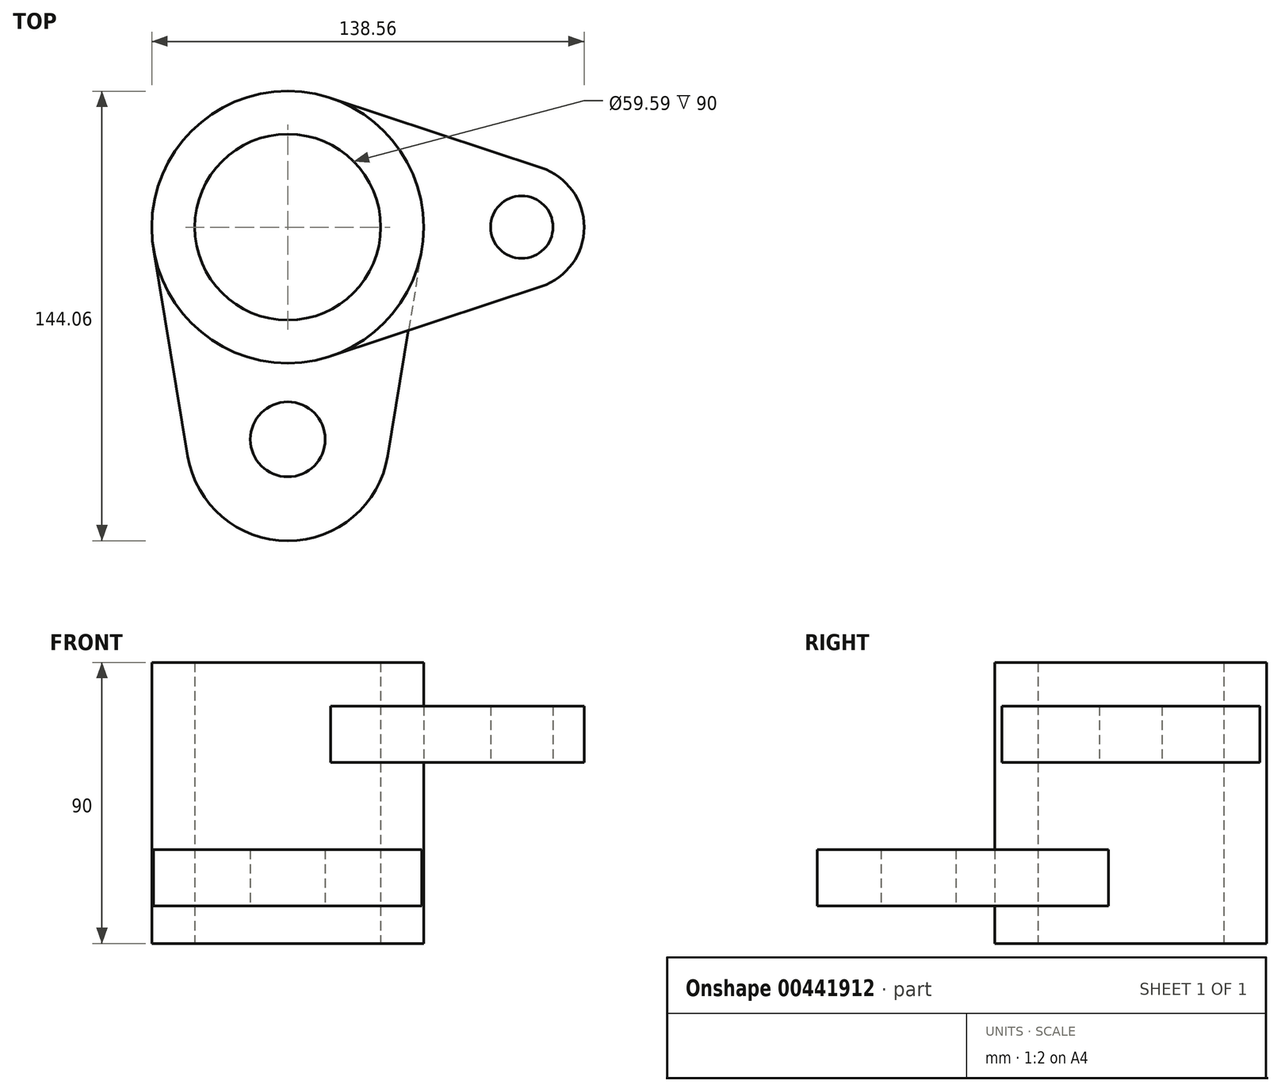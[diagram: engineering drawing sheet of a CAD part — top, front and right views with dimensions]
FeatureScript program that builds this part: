
annotation { "Feature Type Name" : "Feature", "Feature Type Description" : "" }
export const myFeature = defineFeature(function(context is Context, id is Id, definition is map)
    precondition{}
    {
        {
            var Q0;
            Q0=qCreatedBy(makeId("Top.planeOp"),FACE);
            var sketch = newSketch(context, id + "F0", { "sketchPlane" : qUnion([Q0])});
            skCircle(sketch, "E0", {"center": v(0, 0) * mm, "radius": 43.56 * mm});
            skCircle(sketch, "E1", {"center": v(0, 0) * mm, "radius": 29.8 * mm});
            skLineSegment(sketch, "E2", {"start": v(0, -43.56) * mm, "end": v(7.02, -43.56) * mm});
            skArc(sketch, "E3", {"start": v(81.28, -18.99) * mm, "mid": v(95, 0) * mm, "end": v(81.28, 18.99) * mm});
            skLineSegment(sketch, "E4", {"start": v(13.69, 41.36) * mm, "end": v(81.28, 18.99) * mm});
            skLineSegment(sketch, "E5", {"start": v(81.28, -18.99) * mm, "end": v(7.02, -43.56) * mm});
            skPoint(sketch, "E6.orphan", {"position": v(75, 43.56) * mm});
            skPoint(sketch, "E7.orphan", {"position": v(75, -43.56) * mm});
            skPoint(sketch, "E8.visualSharp", {"position": v(138.65, 0) * mm});
            skPoint(sketch, "E9.start.orphan", {"position": v(0, 43.56) * mm});
            skCircle(sketch, "E10", {"center": v(75, 0) * mm, "radius": 10 * mm});
            skSolve(sketch);
        }
        {
            var Q0;
            Q0=makeQuery(id+"F0.imprint","IMPRINT",FACE,{"disambiguationData":[TD([[makeQuery(id+"F0.imprint","IMPRINT",EDGE,{"derivedFrom":sQuery(id+"F0.wireOp",EDGE,"E1")}),-1.0]])]});
            extrude(context, id + "F1", {"entities" : qUnion([Q0]), "depth" : 90 * mm});
        }
        {
            var Q0;
            {var subQ1=sQuery(id+"F0.wireOp",EDGE,"E3");Q0=makeQuery(id+"F0.imprint","IMPRINT",FACE,{"disambiguationData":[TD([[makeQuery(id+"F0.imprint","IMPRINT",EDGE,{"derivedFrom":subQ1}),1.0]])]});}
            extrude(context, id + "F2", {"entities" : qUnion([Q0]), "depth" : 18 * mm});
        }
        {
            var Q0;
            Q0=makeQuery(id+"F2.opExtrude","SWEPT_BODY",BODY,{"disambiguationData":[OSD([sQuery(id+"F0.wireOp",EDGE,"E0"),sQuery(id+"F0.wireOp",EDGE,"E3"),sQuery(id+"F0.wireOp",EDGE,"E4"),sQuery(id+"F0.wireOp",EDGE,"E5"),sQuery(id+"F0.wireOp",EDGE,"E10")])]});
            var Q1;
            Q1=makeQuery(id+"F2.opExtrude","SWEPT_EDGE",EDGE,{"disambiguationData":[OSD([sQuery(id+"F0.wireOp",EDGE,"E3"),sQuery(id+"F0.wireOp",EDGE,"E5")])]});
            transform(context, id + "F3", {"entities" : qUnion([Q0]), "transformType" : TransformType.TRANSLATION_3D, "dx" : 0 * mm, "dy" : 0 * mm, "dz" : (72 - 14) * mm, "makeCopy" : false});
        }
        {
            var Q0;
            Q0=qCreatedBy(makeId("Top.planeOp"),FACE);
            var sketch = newSketch(context, id + "F4", { "sketchPlane" : qUnion([Q0])});
            skPoint(sketch, "E11.0", {"position": v(0, 0) * mm});
            skArc(sketch, "E12", {"start": v(-32.07, -73.29) * mm, "mid": v(0, -100.5) * mm, "end": v(32.07, -73.29) * mm});
            skCircle(sketch, "E13", {"center": v(0, -68) * mm, "radius": 12 * mm});
            skCircle(sketch, "E14.0", {"center": v(0, 0) * mm, "radius": 43.56 * mm});
            skLineSegment(sketch, "E15", {"start": v(-51.61, 45.22) * mm, "end": v(-32.07, -73.29) * mm});
            skLineSegment(sketch, "E16", {"start": v(58.97, 89.84) * mm, "end": v(32.07, -73.29) * mm});
            skSolve(sketch);
        }
        {
            var Q0;
            {var subQ1=sQuery(id+"F4.wireOp",EDGE,"E12");Q0=makeQuery(id+"F4.imprint","IMPRINT",FACE,{"disambiguationData":[TD([[makeQuery(id+"F4.imprint","IMPRINT",EDGE,{"derivedFrom":subQ1}),1.0]])]});}
            extrude(context, id + "F5", {"entities" : qUnion([Q0]), "depth" : 18 * mm});
        }
        {
            var Q0;
            Q0=makeQuery(id+"F5.opExtrude","SWEPT_BODY",BODY,{"disambiguationData":[OSD([sQuery(id+"F4.wireOp",EDGE,"E12"),sQuery(id+"F4.wireOp",EDGE,"E13"),sQuery(id+"F4.wireOp",EDGE,"E14.0"),sQuery(id+"F4.wireOp",EDGE,"E15"),sQuery(id+"F4.wireOp",EDGE,"E16")])]});
            var Q1;
            Q1=makeQuery(id+"F2.opExtrude","SWEPT_EDGE",EDGE,{"disambiguationData":[OSD([sQuery(id+"F0.wireOp",EDGE,"E3"),sQuery(id+"F0.wireOp",EDGE,"E5")])]});
            transform(context, id + "F6", {"entities" : qUnion([Q0]), "transformType" : TransformType.TRANSLATION_3D, "dx" : 0 * mm, "dy" : 0 * mm, "dz" : 12 * mm, "makeCopy" : false});
        }
    });
